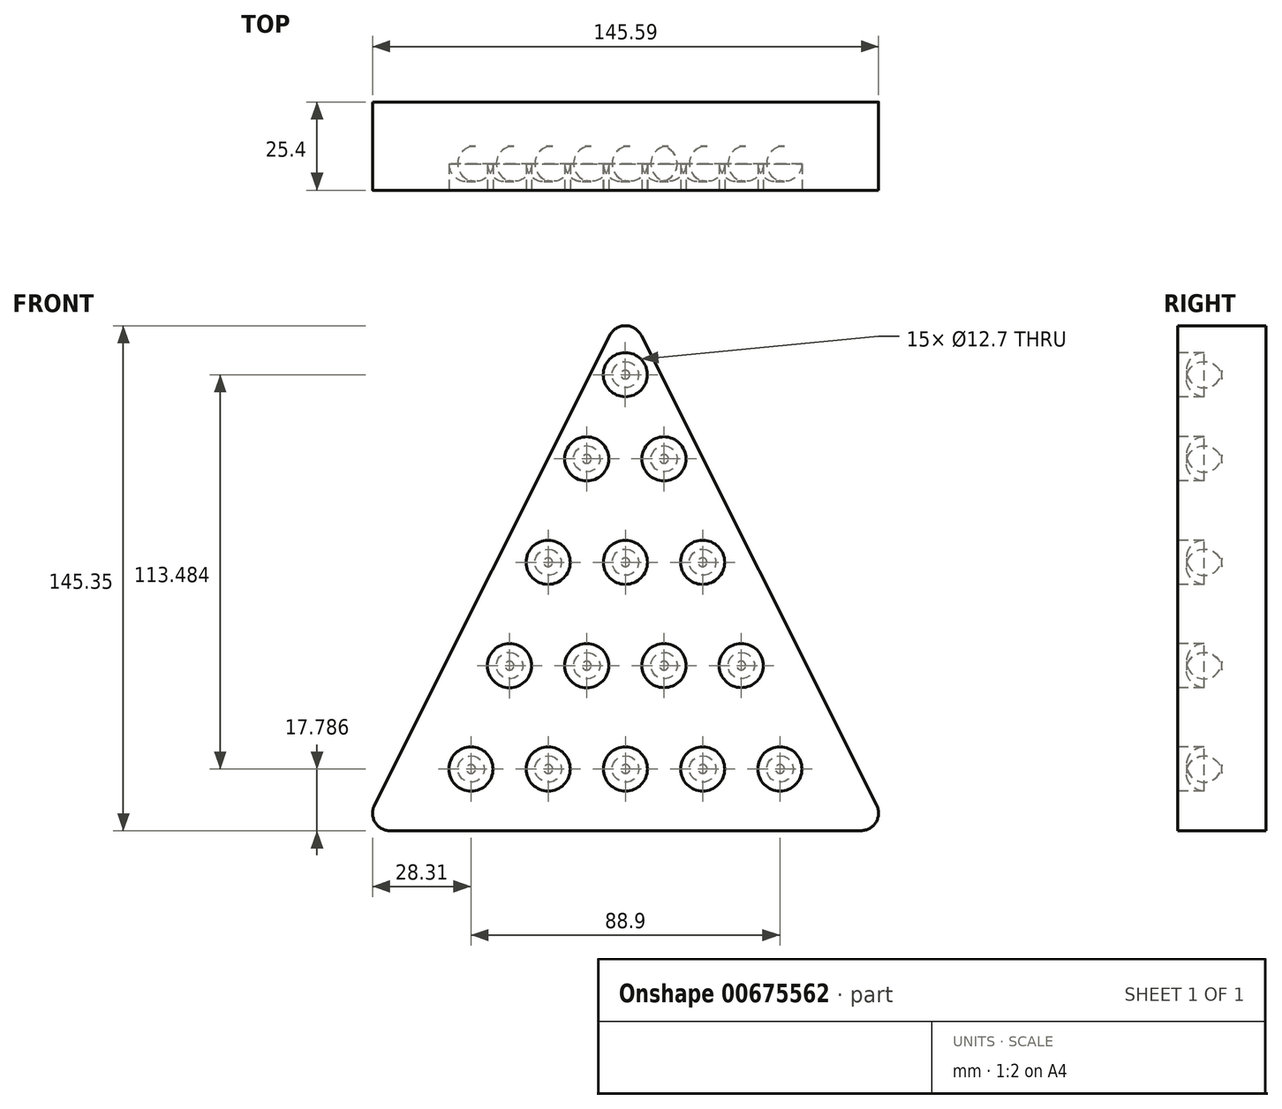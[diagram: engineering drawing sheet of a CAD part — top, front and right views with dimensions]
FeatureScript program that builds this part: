
annotation { "Feature Type Name" : "Feature", "Feature Type Description" : "" }
export const myFeature = defineFeature(function(context is Context, id is Id, definition is map)
    precondition{}
    {
        {
            var Q0;
            Q0=qCreatedBy(makeId("Front.planeOp"),FACE);
            var sketch = newSketch(context, id + "F0", { "sketchPlane" : qUnion([Q0])});
            skLineSegment(sketch, "E0", {"start": v(-75.9, -75.9) * mm, "end": v(0, 75.71) * mm});
            skLineSegment(sketch, "E1", {"start": v(0, 75.71) * mm, "end": v(75.98, -75.86) * mm});
            skLineSegment(sketch, "E2", {"start": v(75.98, -75.86) * mm, "end": v(-75.9, -75.9) * mm});
            skSolve(sketch);
        }
        {
            var Q0;
            Q0 = qSketchRegion(id + "F0", true);
            extrude(context, id + "F1", {"entities" : qUnion([Q0]), "depth" : 25.4 * mm, "offsetDistance" : 25.4 * mm});
        }
        {
            var Q0;
            Q0=makeQuery(id+"F1.opExtrude","CAP_FACE",FACE,{"disambiguationData":[OSD([sQuery(id+"F0.wireOp",EDGE,"E0"),sQuery(id+"F0.wireOp",EDGE,"E1"),sQuery(id+"F0.wireOp",EDGE,"E2")])],"isStart":false});
            var sketch = newSketch(context, id + "F2", { "sketchPlane" : qUnion([Q0])});
            skCircle(sketch, "E3", {"center": v(-44.45, -58.11) * mm, "radius": 6.35 * mm});
            skCircle(sketch, "E4", {"center": v(44.45, -58.09) * mm, "radius": 6.35 * mm});
            skCircle(sketch, "E5", {"center": v(0, -58.1) * mm, "radius": 6.35 * mm});
            skCircle(sketch, "E6", {"center": v(-22.22, -58.1) * mm, "radius": 6.35 * mm});
            skCircle(sketch, "E7", {"center": v(22.22, -58.1) * mm, "radius": 6.35 * mm});
            skSolve(sketch);
        }
        {
            var Q0;
            Q0 = qSketchRegion(id + "F2", true);
            extrude(context, id + "F3", {"entities" : qUnion([Q0]), "operationType" : NewBodyOperationType.REMOVE, "oppositeDirection" : true, "depth" : 12.7 * mm, "offsetDistance" : 25.4 * mm});
        }
        {
            var Q0;
            Q0=makeQuery(id+"F1.opExtrude","CAP_FACE",FACE,{"disambiguationData":[OSD([sQuery(id+"F0.wireOp",EDGE,"E0"),sQuery(id+"F0.wireOp",EDGE,"E1"),sQuery(id+"F0.wireOp",EDGE,"E2")])],"isStart":false});
            var sketch = newSketch(context, id + "F4", { "sketchPlane" : qUnion([Q0])});
            skCircle(sketch, "E8", {"center": v(-33.35, -28.37) * mm, "radius": 6.35 * mm});
            skCircle(sketch, "E9", {"center": v(33.33, -28.35) * mm, "radius": 6.35 * mm});
            skCircle(sketch, "E10", {"center": v(-11.12, -28.36) * mm, "radius": 6.35 * mm});
            skCircle(sketch, "E11", {"center": v(11.1, -28.35) * mm, "radius": 6.35 * mm});
            skSolve(sketch);
        }
        {
            var Q0;
            Q0 = qSketchRegion(id + "F4", true);
            extrude(context, id + "F5", {"entities" : qUnion([Q0]), "operationType" : NewBodyOperationType.REMOVE, "oppositeDirection" : true, "depth" : 12.7 * mm, "offsetDistance" : 25.4 * mm});
        }
        {
            var Q0;
            Q0=makeQuery(id+"F1.opExtrude","CAP_FACE",FACE,{"disambiguationData":[OSD([sQuery(id+"F0.wireOp",EDGE,"E0"),sQuery(id+"F0.wireOp",EDGE,"E1"),sQuery(id+"F0.wireOp",EDGE,"E2")])],"isStart":false});
            var sketch = newSketch(context, id + "F6", { "sketchPlane" : qUnion([Q0])});
            skCircle(sketch, "E12", {"center": v(-22.24, 1.38) * mm, "radius": 6.35 * mm});
            skCircle(sketch, "E13", {"center": v(-0.02, 1.38) * mm, "radius": 6.35 * mm});
            skCircle(sketch, "E14", {"center": v(22.2, 1.4) * mm, "radius": 6.35 * mm});
            skSolve(sketch);
        }
        {
            var Q0;
            Q0 = qSketchRegion(id + "F6", true);
            extrude(context, id + "F7", {"entities" : qUnion([Q0]), "operationType" : NewBodyOperationType.REMOVE, "oppositeDirection" : true, "depth" : 12.7 * mm, "offsetDistance" : 25.4 * mm});
        }
        {
            var Q0;
            Q0=makeQuery(id+"F1.opExtrude","CAP_FACE",FACE,{"disambiguationData":[OSD([sQuery(id+"F0.wireOp",EDGE,"E0"),sQuery(id+"F0.wireOp",EDGE,"E1"),sQuery(id+"F0.wireOp",EDGE,"E2")])],"isStart":false});
            var sketch = newSketch(context, id + "F8", { "sketchPlane" : qUnion([Q0])});
            skCircle(sketch, "E15", {"center": v(-11.14, 31.12) * mm, "radius": 6.35 * mm});
            skCircle(sketch, "E16", {"center": v(11.08, 31.13) * mm, "radius": 6.35 * mm});
            skSolve(sketch);
        }
        {
            var Q0;
            Q0 = qSketchRegion(id + "F8", true);
            extrude(context, id + "F9", {"entities" : qUnion([Q0]), "operationType" : NewBodyOperationType.REMOVE, "oppositeDirection" : true, "depth" : 12.7 * mm, "offsetDistance" : 25.4 * mm});
        }
        {
            var Q0;
            Q0=makeQuery(id+"F1.opExtrude","CAP_FACE",FACE,{"disambiguationData":[OSD([sQuery(id+"F0.wireOp",EDGE,"E0"),sQuery(id+"F0.wireOp",EDGE,"E1"),sQuery(id+"F0.wireOp",EDGE,"E2")])],"isStart":false});
            var sketch = newSketch(context, id + "F10", { "sketchPlane" : qUnion([Q0])});
            skCircle(sketch, "E17", {"center": v(-0.04, 55.37) * mm, "radius": 6.35 * mm});
            skSolve(sketch);
        }
        {
            var Q0;
            Q0 = qSketchRegion(id + "F10", true);
            extrude(context, id + "F11", {"entities" : qUnion([Q0]), "operationType" : NewBodyOperationType.REMOVE, "oppositeDirection" : true, "depth" : 12.7 * mm, "offsetDistance" : 25.4 * mm});
        }
        {
            var Q0;
            Q0=makeQuery(id+"F1.opExtrude","SWEPT_EDGE",EDGE,{"disambiguationData":[OSD([sQuery(id+"F0.wireOp",EDGE,"E0"),sQuery(id+"F0.wireOp",EDGE,"E2")])]});
            fillet(context, id + "F12", {"entities" : qUnion([Q0]), "radius" : 5.08 * mm, "tangentPropagation" : true, "allowEdgeOverflow" : false});
        }
        {
            var Q0;
            Q0=makeQuery(id+"F1.opExtrude","SWEPT_EDGE",EDGE,{"disambiguationData":[OSD([sQuery(id+"F0.wireOp",EDGE,"E1"),sQuery(id+"F0.wireOp",EDGE,"E2")])]});
            fillet(context, id + "F13", {"entities" : qUnion([Q0]), "radius" : 5.08 * mm, "tangentPropagation" : true, "allowEdgeOverflow" : false});
        }
        {
            var Q0;
            Q0=makeQuery(id+"F1.opExtrude","SWEPT_EDGE",EDGE,{"disambiguationData":[OSD([sQuery(id+"F0.wireOp",EDGE,"E0"),sQuery(id+"F0.wireOp",EDGE,"E1")])]});
            fillet(context, id + "F14", {"entities" : qUnion([Q0]), "radius" : 5.08 * mm, "tangentPropagation" : true, "allowEdgeOverflow" : false});
        }
        {
            var Q0;
            Q0=makeQuery(id+"F9.boolean.opBoolean","COPY",FACE,{"derivedFrom":makeQuery(id+"F9.opExtrude","CAP_FACE",FACE,{"disambiguationData":[OSD([sQuery(id+"F8.wireOp",EDGE,"E16")])],"isStart":false})});
            var Q1;
            Q1=makeQuery(id+"F11.boolean.opBoolean","COPY",FACE,{"derivedFrom":makeQuery(id+"F11.opExtrude","CAP_FACE",FACE,{"disambiguationData":[OSD([sQuery(id+"F10.wireOp",EDGE,"E17")])],"isStart":false})});
            var Q2;
            Q2=makeQuery(id+"F9.boolean.opBoolean","COPY",FACE,{"derivedFrom":makeQuery(id+"F9.opExtrude","CAP_FACE",FACE,{"disambiguationData":[OSD([sQuery(id+"F8.wireOp",EDGE,"E15")])],"isStart":false})});
            var Q3;
            Q3=makeQuery(id+"F7.boolean.opBoolean","COPY",FACE,{"derivedFrom":makeQuery(id+"F7.opExtrude","CAP_FACE",FACE,{"disambiguationData":[OSD([sQuery(id+"F6.wireOp",EDGE,"E12")])],"isStart":false})});
            var Q4;
            Q4=makeQuery(id+"F7.boolean.opBoolean","COPY",FACE,{"derivedFrom":makeQuery(id+"F7.opExtrude","CAP_FACE",FACE,{"disambiguationData":[OSD([sQuery(id+"F6.wireOp",EDGE,"E13")])],"isStart":false})});
            var Q5;
            Q5=makeQuery(id+"F7.boolean.opBoolean","COPY",FACE,{"derivedFrom":makeQuery(id+"F7.opExtrude","CAP_FACE",FACE,{"disambiguationData":[OSD([sQuery(id+"F6.wireOp",EDGE,"E14")])],"isStart":false})});
            var Q6;
            Q6=makeQuery(id+"F5.boolean.opBoolean","COPY",FACE,{"derivedFrom":makeQuery(id+"F5.opExtrude","CAP_FACE",FACE,{"disambiguationData":[OSD([sQuery(id+"F4.wireOp",EDGE,"E9")])],"isStart":false})});
            var Q7;
            Q7=makeQuery(id+"F5.boolean.opBoolean","COPY",FACE,{"derivedFrom":makeQuery(id+"F5.opExtrude","CAP_FACE",FACE,{"disambiguationData":[OSD([sQuery(id+"F4.wireOp",EDGE,"E11")])],"isStart":false})});
            var Q8;
            Q8=makeQuery(id+"F5.boolean.opBoolean","COPY",FACE,{"derivedFrom":makeQuery(id+"F5.opExtrude","CAP_FACE",FACE,{"disambiguationData":[OSD([sQuery(id+"F4.wireOp",EDGE,"E10")])],"isStart":false})});
            var Q9;
            Q9=makeQuery(id+"F5.boolean.opBoolean","COPY",FACE,{"derivedFrom":makeQuery(id+"F5.opExtrude","CAP_FACE",FACE,{"disambiguationData":[OSD([sQuery(id+"F4.wireOp",EDGE,"E8")])],"isStart":false})});
            var Q10;
            Q10=makeQuery(id+"F3.boolean.opBoolean","COPY",FACE,{"derivedFrom":makeQuery(id+"F3.opExtrude","CAP_FACE",FACE,{"disambiguationData":[OSD([sQuery(id+"F2.wireOp",EDGE,"E4")])],"isStart":false})});
            var Q11;
            Q11=makeQuery(id+"F3.boolean.opBoolean","COPY",EDGE,{"derivedFrom":makeQuery(id+"F3.opExtrude","CAP_EDGE",EDGE,{"disambiguationData":[OSD([sQuery(id+"F2.wireOp",EDGE,"E7")])],"isStart":false})});
            var Q12;
            Q12=makeQuery(id+"F3.boolean.opBoolean","COPY",EDGE,{"derivedFrom":makeQuery(id+"F3.opExtrude","CAP_EDGE",EDGE,{"disambiguationData":[OSD([sQuery(id+"F2.wireOp",EDGE,"E5")])],"isStart":false})});
            var Q13;
            Q13=makeQuery(id+"F3.boolean.opBoolean","COPY",EDGE,{"derivedFrom":makeQuery(id+"F3.opExtrude","CAP_EDGE",EDGE,{"disambiguationData":[OSD([sQuery(id+"F2.wireOp",EDGE,"E6")])],"isStart":false})});
            var Q14;
            Q14=makeQuery(id+"F3.boolean.opBoolean","COPY",FACE,{"derivedFrom":makeQuery(id+"F3.opExtrude","CAP_FACE",FACE,{"disambiguationData":[OSD([sQuery(id+"F2.wireOp",EDGE,"E3")])],"isStart":false})});
            fillet(context, id + "F15", {"entities" : qUnion([Q0, Q1, Q2, Q3, Q4, Q5, Q6, Q7, Q8, Q9, Q10, Q11, Q12, Q13, Q14]), "radius" : 5.08 * mm, "tangentPropagation" : true, "allowEdgeOverflow" : false});
        }
    });
